# Revit family: Haworth_Masters_AttachedStorage
name_source: partatom
category: Furniture Systems
revit_build: Autodesk Revit 2018 (Build: 20170223_1515(x64)
units: mm (PartAtom-declared; Revit-internal decimal feet)

## family parameters
Always vertical = Yes
Cut with Voids When Loaded = No
OmniClass Number = 23.40.70.14.64.21
OmniClass Title = Systems Furniture
Part Type = Normal
Room Calculation Point = No
Round Connector Dimension = Use Diameter
Shared = No
Work Plane-Based = No

## types (7) — shared parameters
Actual Depth = 18"
Actual Width = 35 7/8"
Assembly Code = E2020200
Bar Pull = Yes
Bar Pull Door = 11 15/16"
Bar Pull Drawer = 29 7/8"
Cabinet Depth = 18"
Cabinet Finish = Haworth _ Wood _ White Oak
Classic Pull = No
Custom Size = No
Depth = 18"
Description = Haworth - Masters - Attached Storage
Door Width = 17 7/8"
Drawer Height = 13"
Finger Pull = No
Finished Back = No
Front Finish = Haworth _ Wood _ White Oak
Hardware Finish = Haworth _ Metal _ Brushed Aluminum
Linear Pull = No
Manufacturer = Haworth
Max. Height = 63 1/2"
Max. Width = 47 7/8"
Min. Height = 27 1/2"
Min. Width = 29 7/8"
Model = Haworth - Masters - Attached Storage
Revision Number = 3
Size = Verify Final Dim. w/ Haworth
Standard Depths = 18, 23 in.
Standard Widths = 30, 36 in.
Sustainability Info = http://www.haworth.com
Top Open Shelf = No
Touch Latch = No
URL = www.haworth.com
URL - Product = http://www.haworth.com
Warranty = http://www.haworth.com
Width = 36"

## per-type parameters (varying)
| type | Actual Doors | Actual Drawers | Actual Height | Door Height | Doors | Drawers | One High | One and One Half High | Open | Shelf | Top Drawer | Top Drawer Height | Two High |
| Lateral - Two High - 36w | No | Yes | 28" | 26 1/8" | No | Yes | No | No | No | Yes | Yes | 13" | Yes |
| Lateral - One High - 36w | No | Yes | 15 3/16" | 13 5/16" | No | Yes | Yes | No | No | No | No | 6 1/4" | No |
| Open - Two High - 36w | No | No | 28" | 26 1/8" | No | No | No | No | Yes | Yes | No | 13" | Yes |
| Open - One High - 36w | No | No | 15 3/16" | 13 5/16" | No | No | Yes | No | Yes | No | No | 6 1/4" | No |
| Doors - Two High - 36w | Yes | No | 28" | 26 1/8" | Yes | No | No | No | No | Yes | No | 13" | Yes |
| Open - One and One Half High - 36w | No | No | 21 5/8" | 19 3/4" | No | No | No | Yes | Yes | Yes | No | 6 1/4" | No |
| Lateral - One and One Half High - 36w | No | Yes | 21 5/8" | 19 3/4" | No | Yes | No | Yes | No | Yes | Yes | 6 1/4" | No |

## geometry (parser evidence)
native form markers: Sweep x12
no freeform markers — native parametric forms only
